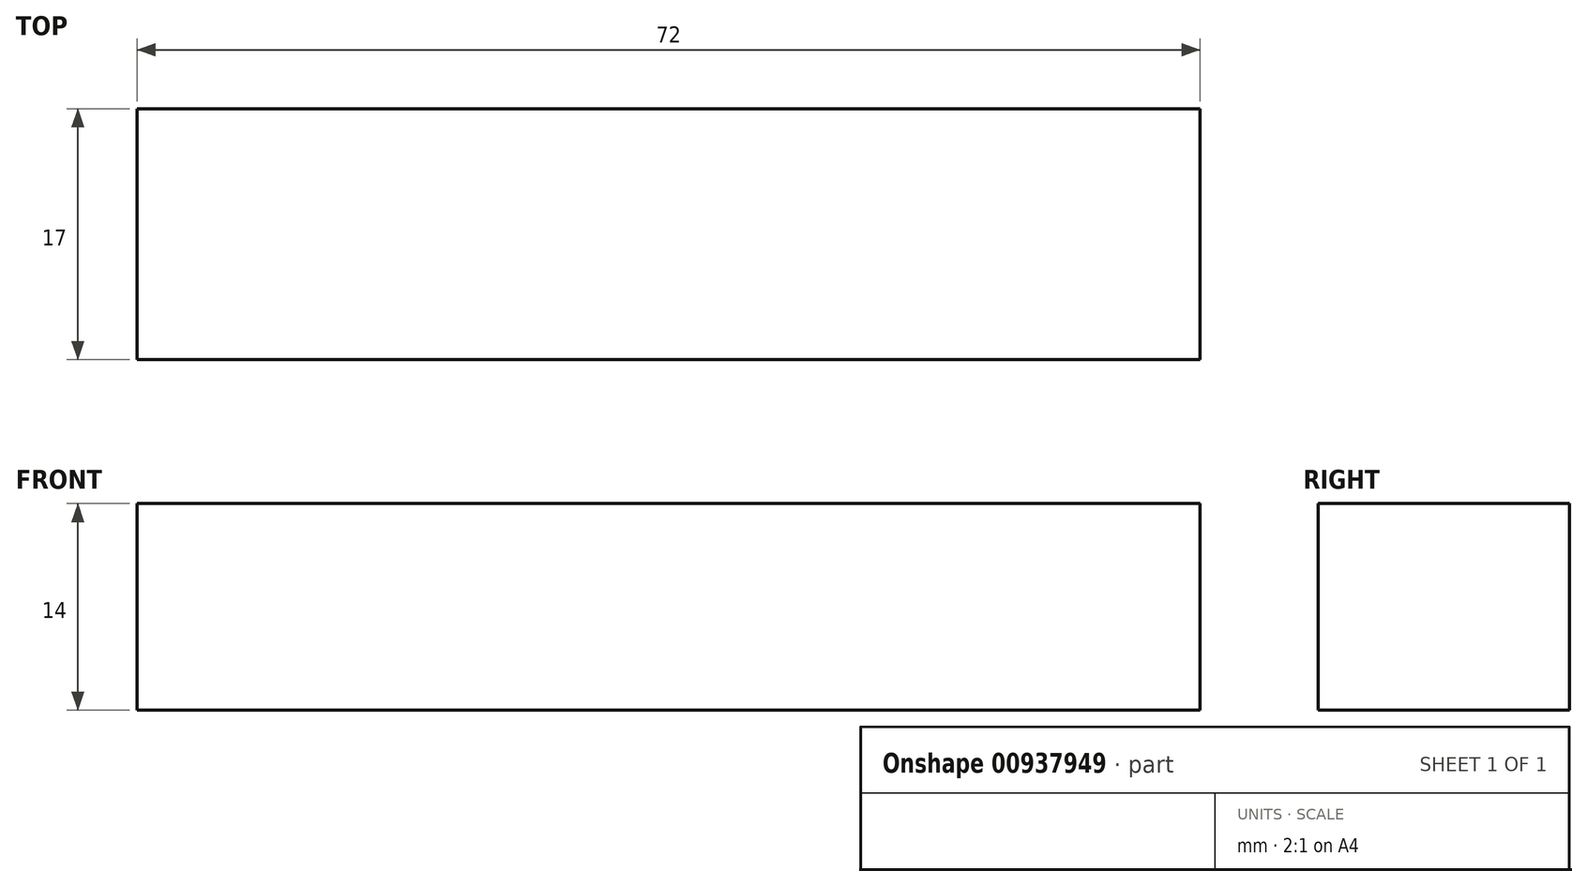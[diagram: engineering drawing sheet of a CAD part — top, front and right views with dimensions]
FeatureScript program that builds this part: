
annotation { "Feature Type Name" : "Feature", "Feature Type Description" : "" }
export const myFeature = defineFeature(function(context is Context, id is Id, definition is map)
    precondition{}
    {
        {
            var Q0;
            Q0=qCreatedBy(makeId("Top.planeOp"),FACE);
            var sketch = newSketch(context, id + "F0", { "sketchPlane" : qUnion([Q0])});
            skLineSegment(sketch, "E0.bottom", {"start": v(-47.8, 26.22) * mm, "end": v(24.2, 26.22) * mm});
            skLineSegment(sketch, "E0.top", {"start": v(-47.8, 9.22) * mm, "end": v(24.2, 9.22) * mm});
            skLineSegment(sketch, "E0.left", {"start": v(-47.8, 26.22) * mm, "end": v(-47.8, 9.22) * mm});
            skLineSegment(sketch, "E0.right", {"start": v(24.2, 26.22) * mm, "end": v(24.2, 9.22) * mm});
            skSolve(sketch);
        }
        {
            var Q0;
            Q0=makeQuery(id+"F0.imprint","IMPRINT",FACE,{"disambiguationData":[TD([[makeQuery(id+"F0.imprint","IMPRINT",EDGE,{"derivedFrom":sQuery(id+"F0.wireOp",EDGE,"E0.bottom")}),-1.0]])]});
            extrude(context, id + "F1", {"entities" : qUnion([Q0]), "depth" : 14 * mm, "offsetDistance" : 25.4 * mm});
        }
    });
